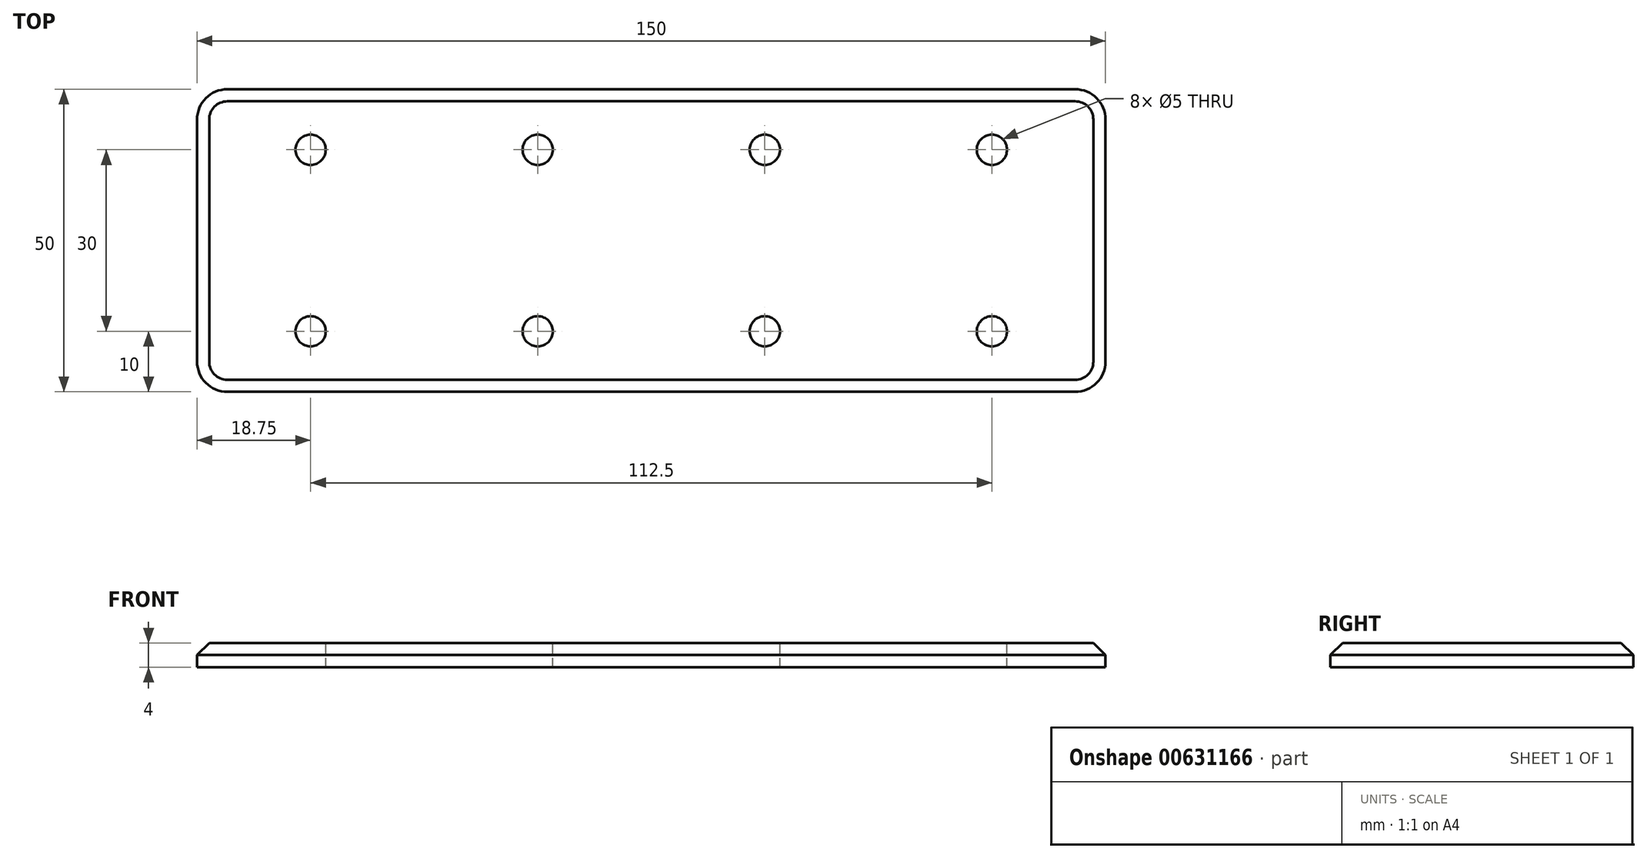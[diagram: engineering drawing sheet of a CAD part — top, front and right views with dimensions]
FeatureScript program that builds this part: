
annotation { "Feature Type Name" : "Feature", "Feature Type Description" : "" }
export const myFeature = defineFeature(function(context is Context, id is Id, definition is map)
    precondition{}
    {
        {
            var Q0;
            Q0=qCreatedBy(makeId("Top.planeOp"),FACE);
            var sketch = newSketch(context, id + "F0", { "sketchPlane" : qUnion([Q0])});
            skLineSegment(sketch, "E0.bottom", {"start": v(75, 25) * mm, "end": v(-75, 25) * mm});
            skLineSegment(sketch, "E0.top", {"start": v(75, -25) * mm, "end": v(-75, -25) * mm});
            skLineSegment(sketch, "E0.left", {"start": v(75, 25) * mm, "end": v(75, -25) * mm});
            skLineSegment(sketch, "E0.right", {"start": v(-75, 25) * mm, "end": v(-75, -25) * mm});
            skPoint(sketch, "E0.middle", {"position": v(0, 0) * mm});
            skSolve(sketch);
        }
        {
            var Q0;
            Q0 = qSketchRegion(id + "F0", true);
            extrude(context, id + "F1", {"entities" : qUnion([Q0]), "depth" : 4 * mm, "offsetDistance" : 25 * mm});
        }
        {
            var Q0;
            Q0=makeQuery(id+"F1.opExtrude","CAP_FACE",FACE,{"disambiguationData":[OSD([sQuery(id+"F0.wireOp",EDGE,"E0.bottom"),sQuery(id+"F0.wireOp",EDGE,"E0.top"),sQuery(id+"F0.wireOp",EDGE,"E0.left"),sQuery(id+"F0.wireOp",EDGE,"E0.right")])],"isStart":false});
            var sketch = newSketch(context, id + "F2", { "sketchPlane" : qUnion([Q0])});
            skPoint(sketch, "E1", {"position": v(-56.25, 15) * mm});
            skPoint(sketch, "E2.MirrorP", {"position": v(-56.25, -15) * mm});
            skPoint(sketch, "E3.MirrorP", {"position": v(56.25, 15) * mm});
            skPoint(sketch, "E4.MirrorP", {"position": v(56.25, -15) * mm});
            skPoint(sketch, "E5.MirrorP", {"position": v(-18.75, 15) * mm});
            skPoint(sketch, "E6.MirrorP", {"position": v(-18.75, -15) * mm});
            skPoint(sketch, "E7.MirrorP", {"position": v(18.75, 15) * mm});
            skPoint(sketch, "E8.MirrorP", {"position": v(18.75, -15) * mm});
            skSolve(sketch);
        }
        {
            var Q0;
            Q0=sQuery(id+"F2.wireOp",VERTEX,"E1");
            var Q1;
            Q1=sQuery(id+"F2.wireOp",VERTEX,"E2.MirrorP");
            var Q2;
            Q2=sQuery(id+"F2.wireOp",VERTEX,"E6.MirrorP");
            var Q3;
            Q3=sQuery(id+"F2.wireOp",VERTEX,"E5.MirrorP");
            var Q4;
            Q4=sQuery(id+"F2.wireOp",VERTEX,"E7.MirrorP");
            var Q5;
            Q5=sQuery(id+"F2.wireOp",VERTEX,"E8.MirrorP");
            var Q6;
            Q6=sQuery(id+"F2.wireOp",VERTEX,"E4.MirrorP");
            var Q7;
            Q7=sQuery(id+"F2.wireOp",VERTEX,"E3.MirrorP");
            var Q8;
            Q8=makeQuery(id+"F1.opExtrude","SWEPT_BODY",BODY,{"disambiguationData":[OSD([sQuery(id+"F0.wireOp",EDGE,"E0.bottom"),sQuery(id+"F0.wireOp",EDGE,"E0.top"),sQuery(id+"F0.wireOp",EDGE,"E0.left"),sQuery(id+"F0.wireOp",EDGE,"E0.right")])]});
            hole(context, id + "F3", {"style" : HoleStyle.SIMPLE, "endStyle" : HoleEndStyle.THROUGH, "holeDiameter" : 5 * mm, "majorDiameter" : 5 * mm, "isTappedThrough" : true, "tappedDepth" : 12 * mm, "tapClearance" : 3, "locations" : qUnion([Q0, Q1, Q2, Q3, Q4, Q5, Q6, Q7]), "scope" : qUnion([Q8])});
        }
        {
            var Q0;
            Q0=makeQuery(id+"F1.opExtrude","SWEPT_EDGE",EDGE,{"disambiguationData":[OSD([sQuery(id+"F0.wireOp",EDGE,"E0.bottom"),sQuery(id+"F0.wireOp",EDGE,"E0.right")])]});
            var Q1;
            Q1=makeQuery(id+"F1.opExtrude","SWEPT_EDGE",EDGE,{"disambiguationData":[OSD([sQuery(id+"F0.wireOp",EDGE,"E0.top"),sQuery(id+"F0.wireOp",EDGE,"E0.right")])]});
            var Q2;
            Q2=makeQuery(id+"F1.opExtrude","SWEPT_EDGE",EDGE,{"disambiguationData":[OSD([sQuery(id+"F0.wireOp",EDGE,"E0.top"),sQuery(id+"F0.wireOp",EDGE,"E0.left")])]});
            var Q3;
            Q3=makeQuery(id+"F1.opExtrude","SWEPT_EDGE",EDGE,{"disambiguationData":[OSD([sQuery(id+"F0.wireOp",EDGE,"E0.bottom"),sQuery(id+"F0.wireOp",EDGE,"E0.left")])]});
            fillet(context, id + "F4", {"entities" : qUnion([Q0, Q1, Q2, Q3]), "radius" : 5 * mm, "tangentPropagation" : true, "allowEdgeOverflow" : false});
        }
        {
            var Q0;
            Q0=makeQuery(id+"F1.opExtrude","CAP_EDGE",EDGE,{"disambiguationData":[OSD([sQuery(id+"F0.wireOp",EDGE,"E0.top")])],"isStart":false});
            chamfer(context, id + "F5", {"entities" : qUnion([Q0]), "width" : 2 * mm, "tangentPropagation" : true});
        }
    });
